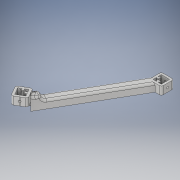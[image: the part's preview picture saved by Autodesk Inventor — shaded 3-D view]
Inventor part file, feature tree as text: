
AUTODESK INVENTOR PART (.ipt)
format: ipt  version: 2019.4 (Build 234330000, 330)  size: 515,584 bytes
history: native  units: mm
features: sketch x14, extrude x13, fillet x11
ambient origin geometry x8: Origin, YZ Plane, XZ Plane, XY Plane, X Axis, Y Axis, Z Axis, Center Point
bodies: Body1 (feature_tree)
feature tree (38):
  extrude  "Extrusion7"  TaperAngle=90.0deg  [1 undecoded]
  sketch  "Sketch7"  dims[d57=21.0mm d58=21.0mm d59=10.0mm]
  extrude  "Extrusion10"  Depth=21.0mm
  fillet  "Fillet2"  Radius=10.0mm
  extrude  "Extrusion11"  Depth=32.0mm
  extrude  "Extrusion13"  Depth=20.0mm TaperAngle=0.0deg
  fillet  "Fillet3"  Radius=10.0mm
  extrude  "Extrusion14"  TaperAngle=270.0deg  [1 undecoded]
  fillet  "Fillet4"  Radius=2.5mm
  fillet  "Fillet5"  Radius=2.5mm
  fillet  "Fillet6"  Radius=4.8mm
  fillet  "Fillet7"  Radius=10.0mm
  fillet  "Fillet8"  Radius=5.0mm
  fillet  "Fillet9"  [1 undecoded]
  fillet  "Fillet10"  Radius=5.0mm
  extrude  "Extrusion15"  Depth=10.5mm
  extrude  "Extrusion16"  Depth=1.0mm TaperAngle=360.0deg
  extrude  "Extrusion17"  Depth=0.5mm
  extrude  "Extrusion19"  TaperAngle=30.0deg  [1 undecoded]
  extrude  "Extrusion20"  Depth=4.8mm
  extrude  "Extrusion21"  TaperAngle=90.0deg  [1 undecoded]
  fillet  "Fillet11"  Radius=10.5mm
  fillet  "Fillet12"  Radius=1.0mm
  extrude  "Extrusion22"  TaperAngle=165.0deg  [1 undecoded]
  extrude  "Extrusion23"  Depth=1.0mm
  sketch  "Sketch6"  dims[d55=150.0mm d56=90.0deg]
  sketch  "Sketch10"  dims[d60=32.0mm d61=32.0mm]
  sketch  "Sketch11"  dims[d62=30.0mm d64=360.0deg d66=20.0mm d67=0.0mm d68=10.0mm]
  sketch  "Sketch13"  dims[d84=1.0mm d85=270.0deg d86=2.5mm d87=2.5mm d88=4.8mm d89=10.0mm d90=5.0mm d91=45.0deg d92=5.0mm]
  sketch  "Sketch14"  dims[d93=135.0deg d94=10.5mm]
  sketch  "Sketch15"  dims[d95=1.0mm d96=40.0mm d98=360.0deg]
  sketch  "Sketch16"  dims[d100=20.0mm d101=0.0mm d102=0.5mm]
  sketch  "Sketch17"  dims[d103=10.5mm d104=30.0deg]
  sketch  "Sketch18"  dims[d105=11.0mm d106=4.8mm]
  sketch  "Sketch19"  dims[d107=1.0mm d108=90.0deg d109=10.5mm d110=1.0mm]
  sketch  "Sketch20"  dims[d111=4.0mm d112=165.0deg]
  sketch  "Sketch21"  dims[d113=4.0mm d114=1.0mm]
  sketch  "Sketch22"  dims[d115=40.0mm d117=360.0deg d119=27.712813mm d120=27.712813mm d121=16.0mm d122=21.0mm d123=20.0mm d124=0.0mm d127=20.0mm d128=10.0mm d129=0.0mm d130=10.0mm d131=33.0mm d132=120.0deg d133=33.0mm d134=20.0mm d135=0.0mm d136=5.0mm d137=1.0mm d138=1.0mm d139=5.0mm d140=5.0mm d141=5.0mm d142=5.0mm d143=13.0mm d144=6.0mm d145=6.0mm d146=13.0mm d147=20.0mm d148=0.0mm d149=10.0mm d150=5.5mm d151=5.5mm d152=0.0mm d153=5.5mm d154=5.5mm d155=0.0mm d158=13.0mm d159=6.0mm d162=20.0mm d163=0.0mm d164=13.0mm d165=6.0mm d166=10.0mm d167=5.5mm d168=5.5mm d169=0.0mm d170=10.0mm d171=90.0deg d172=5.5mm d173=10.0mm d174=0.0mm d175=5.0mm d176=0.5mm d177=21.0mm d178=30.0deg d179=1.0mm d180=1.0mm d181=0.0mm d182=21.0mm d183=1.0mm d184=1.0mm d185=0.0mm]
note: 6 required parameter values undecoded (feature->parameter linkage not recoverable at this tier; creation-order binding heuristic only, values carry confidence <= 0.55)
